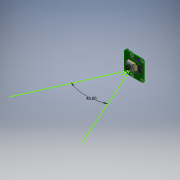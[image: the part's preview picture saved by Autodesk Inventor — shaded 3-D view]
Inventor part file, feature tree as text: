
AUTODESK INVENTOR PART (.ipt)
format: ipt  version: 2017 (Build 210142000, 142)  size: 4,349,440 bytes
history: native  units: in
note: dims shown in document units (in); Inventor stores cm internally (conversion verified against a paired STEP export)
features: other x129, sketch x2
ambient origin geometry x8: Origin, YZ Plane, XZ Plane, XY Plane, X Axis, Y Axis, Z Axis, Center Point
bodies: Solid1 (feature_tree), Solid2 (feature_tree), Solid3 (feature_tree), Solid4 (feature_tree), Solid5 (feature_tree), Solid6 (feature_tree), Solid7 (feature_tree), Solid8 (feature_tree), Solid9 (feature_tree), Solid10 (feature_tree), Solid11 (feature_tree), Solid12 (feature_tree), Solid13 (feature_tree), Solid14 (feature_tree), Solid15 (feature_tree), Solid16 (feature_tree), Solid17 (feature_tree), Solid18 (feature_tree), Solid19 (feature_tree), Solid20 (feature_tree), Solid21 (feature_tree), Solid22 (feature_tree), Solid23 (feature_tree), Solid24 (feature_tree), Solid25 (feature_tree), Solid26 (feature_tree), Solid27 (feature_tree), Solid28 (feature_tree), Solid29 (feature_tree), Solid30 (feature_tree), Solid31 (feature_tree), Solid32 (feature_tree), Solid33 (feature_tree), Solid34 (feature_tree), Solid35 (feature_tree), Solid36 (feature_tree), Solid37 (feature_tree), Solid38 (feature_tree), Solid39 (feature_tree), Solid40 (feature_tree), Solid41 (feature_tree), Solid42 (feature_tree), Solid43 (feature_tree), Solid44 (feature_tree), Solid45 (feature_tree), Solid46 (feature_tree), Solid47 (feature_tree), Solid48 (feature_tree), Solid49 (feature_tree), Solid50 (feature_tree), Solid51 (feature_tree), Solid52 (feature_tree), Solid53 (feature_tree), Solid54 (feature_tree), Solid55 (feature_tree), Solid56 (feature_tree), Solid57 (feature_tree), Solid58 (feature_tree), Solid59 (feature_tree), Solid60 (feature_tree), Solid61 (feature_tree), Solid62 (feature_tree), Solid63 (feature_tree), Solid64 (feature_tree), Solid65 (feature_tree), Solid66 (feature_tree), Solid67 (feature_tree), Solid68 (feature_tree), Solid69 (feature_tree), Solid70 (feature_tree), Solid71 (feature_tree), Solid72 (feature_tree), Solid73 (feature_tree), Solid74 (feature_tree), Solid75 (feature_tree), Solid76 (feature_tree), Solid77 (feature_tree), Solid78 (feature_tree), Solid79 (feature_tree), Solid80 (feature_tree), Solid81 (feature_tree), Solid82 (feature_tree), Solid83 (feature_tree), Solid84 (feature_tree), Solid85 (feature_tree), Solid86 (feature_tree), Solid87 (feature_tree), Solid88 (feature_tree), Solid89 (feature_tree), Solid90 (feature_tree), Solid91 (feature_tree), Solid92 (feature_tree), Solid93 (feature_tree), Solid94 (feature_tree), Solid95 (feature_tree), Solid96 (feature_tree), Solid97 (feature_tree), Solid98 (feature_tree), Solid99 (feature_tree), Solid100 (feature_tree), Solid101 (feature_tree), Solid102 (feature_tree), Solid103 (feature_tree), Solid104 (feature_tree), Solid105 (feature_tree), Solid106 (feature_tree), Solid107 (feature_tree), Solid108 (feature_tree), Solid109 (feature_tree), Solid110 (feature_tree), Solid111 (feature_tree), Solid112 (feature_tree), Solid113 (feature_tree), Solid114 (feature_tree), Solid115 (feature_tree), Solid116 (feature_tree), Solid117 (feature_tree), Solid118 (feature_tree), Solid119 (feature_tree), Solid120 (feature_tree), Solid121 (feature_tree), Solid122 (feature_tree), Solid123 (feature_tree), Solid124 (feature_tree), Solid125 (feature_tree), Solid126 (feature_tree), Solid127 (feature_tree), Solid128 (feature_tree), Solid129 (feature_tree), Solid130 (feature_tree), Solid131 (feature_tree), Solid132 (feature_tree), Solid133 (feature_tree)
feature tree (131):
  other  "Repaired Geometry1"
  sketch  "Sketch1"  dims[d0=0.3298in]
  sketch  "3D Sketch1"
  other  "PicameraPCB_1:1"
  other  "PicameraPCB_1:2"
  other  "PicameraPCB_1:3"
  other  "PicameraPCB_1:4"
  other  "PicameraPCB_1:5"
  other  "PicameraPCB_1:6"
  other  "PicameraPCB_1:7"
  other  "PicameraPCB_1:8"
  other  "PicameraPCB_1:9"
  other  "PicameraPCB_1:10"
  other  "PicameraPCB_1:11"
  other  "PicameraPCB_1:12"
  other  "PicameraPCB_1:13"
  other  "PicameraPCB_1:14"
  other  "PicameraPCB_1:15"
  other  "PicameraPCB_1:16"
  other  "PicameraPCB_1:17"
  other  "PicameraPCB_1:18"
  other  "PicameraPCB_1:19"
  other  "PicameraPCB_1:20"
  other  "PicameraPCB_1:21"
  other  "PicameraPCB_1:22"
  other  "PicameraPCB_1:23"
  other  "PicameraPCB_1:24"
  other  "PicameraPCB_1:25"
  other  "PicameraPCB_1:26"
  other  "PicameraPCB_1:27"
  other  "PicameraPCB_1:28"
  other  "PicameraPCB_1:29"
  other  "PicameraPCB_1:30"
  other  "PicameraPCB_1:31"
  other  "PicameraPCB_1:32"
  other  "PicameraPCB_1:33"
  other  "PicameraPCB_1:34"
  other  "PicameraPCB_1:35"
  other  "PicameraPCB_1:36"
  other  "PicameraPCB_1:37"
  other  "PicameraPCB_1:38"
  other  "PicameraPCB_1:39"
  other  "PicameraPCB_1:40"
  other  "PicameraPCB_1:41"
  other  "PicameraPCB_1:42"
  other  "PicameraPCB_1:43"
  other  "PicameraPCB_1:44"
  other  "PicameraPCB_1:45"
  other  "PicameraPCB_1:46"
  other  "PicameraPCB_1:47"
  other  "PicameraPCB_1:48"
  other  "PicameraPCB_1:49"
  other  "OVA5647_Housing_1:1"
  other  "OVA5647_Lens_FOV_1:1"
  other  "ribbon_cam_1:1"
  other  "CAPC-0805-T0.75-BN_1:1"
  other  "CAPC-0805-T0.75-BN_2:1"
  other  "CAPC-0402-T0.55-BN_1:1"
  other  "CAPC-0402-T0.55-BN_2:1"
  other  "CAPC-0402-T0.55-BN_3:1"
  other  "CAPC-0402-T0.55-BN_4:1"
  other  "CAPC-0402-T0.55-BN_5:1"
  other  "CAPC-0402-T0.55-BN_6:1"
  other  "CAPC-0402-T0.55-BN_7:1"
  other  "CAPC-0402-T0.55-BN_8:1"
  other  "CAPC-0402-T0.55-BN_9:1"
  other  "CAPC-0402-T0.55-BN_10:1"
  other  "RESC-0402_1:1"
  other  "RESC-0402_1:2"
  other  "RESC-0402_1:3"
  other  "RESC-0402_2:1"
  other  "RESC-0402_2:2"
  other  "RESC-0402_2:3"
  other  "RESC-0402_5:1"
  other  "RESC-0402_5:2"
  other  "RESC-0402_5:3"
  other  "RESC-0603_1:1"
  other  "RESC-0603_1:2"
  other  "RESC-0603_1:3"
  other  "RESC-0603_2:1"
  other  "RESC-0603_2:2"
  other  "RESC-0603_2:3"
  other  "RESC-1210_1:1"
  other  "RESC-1210_1:2"
  other  "RESC-1210_1:3"
  other  "c-1-1734248-5-e-raspberry_display_1:1"
  other  "SOT23-5_1:1"
  other  "SOT23-5_1:2"
  other  "SOT23-5_1:3"
  other  "SOT23-5_1:4"
  other  "SOT23-5_1:5"
  other  "SOT23-5_1:6"
  other  "SOT23-5_2:1"
  other  "SOT23-5_2:2"
  other  "SOT23-5_2:3"
  other  "SOT23-5_2:4"
  other  "SOT23-5_2:5"
  other  "SOT23-5_2:6"
  other  "SOT23-5_3:1"
  other  "SOT23-5_3:2"
  other  "SOT23-5_3:3"
  other  "SOT23-5_3:4"
  other  "SOT23-5_3:5"
  other  "SOT23-5_3:6"
  other  "KX7 SMD Quartz Crystal Resonator 3.2x2.5mm_4:1"
  other  "c6aaa_1:1"
  other  "c6aaa_1:2"
  other  "c6aaa_1:3"
  other  "c6aaa_1:4"
  other  "c6aaa_1:5"
  other  "c6aaa_1:6"
  other  "c6aaa_1:7"
  other  "c6aaa_1:8"
  other  "c6aaa_1:9"
  other  "4pin_smd_1:1"
  other  "4pin_smd_1:2"
  other  "4pin_smd_1:3"
  other  "4pin_smd_1:4"
  other  "4pin_smd_1:5"
  other  "4pin_smd_2:1"
  other  "4pin_smd_2:2"
  other  "4pin_smd_2:3"
  other  "4pin_smd_2:4"
  other  "4pin_smd_2:5"
  other  "4pin_smd_3:1"
  other  "4pin_smd_3:2"
  other  "4pin_smd_3:3"
  other  "4pin_smd_3:4"
  other  "4pin_smd_3:5"
  other  "Composite1"
  other  "Srf1"
